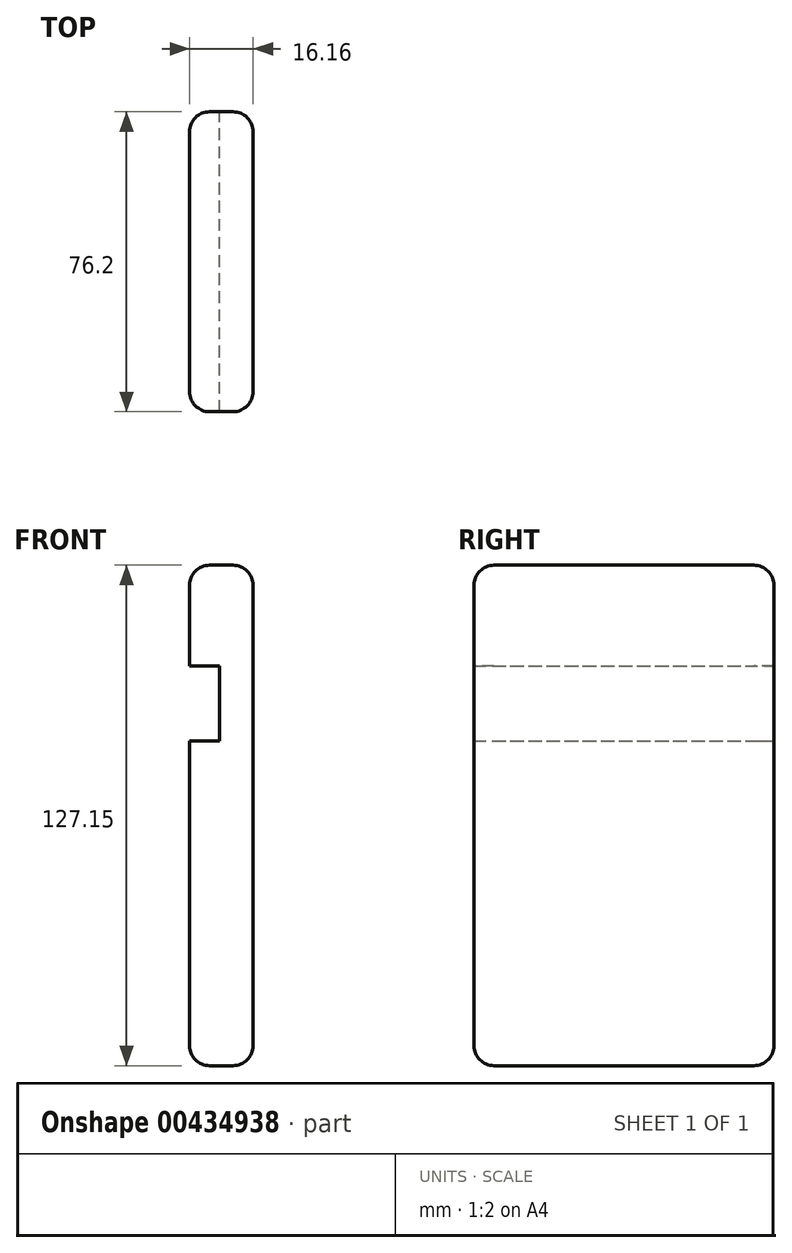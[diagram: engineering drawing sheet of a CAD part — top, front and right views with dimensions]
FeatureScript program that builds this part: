
annotation { "Feature Type Name" : "Feature", "Feature Type Description" : "" }
export const myFeature = defineFeature(function(context is Context, id is Id, definition is map)
    precondition{}
    {
        {
            var Q0;
            Q0=qCreatedBy(makeId("Front.planeOp"),FACE);
            var sketch = newSketch(context, id + "F0", { "sketchPlane" : qUnion([Q0])});
            skLineSegment(sketch, "E0", {"start": v(0, 0) * mm, "end": v(0, 127.15) * mm});
            skLineSegment(sketch, "E1", {"start": v(0, 127.15) * mm, "end": v(-16.16, 127.15) * mm});
            skLineSegment(sketch, "E2", {"start": v(-16.16, 127.15) * mm, "end": v(-16.16, 101.6) * mm});
            skLineSegment(sketch, "E3", {"start": v(-16.16, 101.6) * mm, "end": v(-8.54, 101.6) * mm});
            skLineSegment(sketch, "E4", {"start": v(-8.54, 101.6) * mm, "end": v(-8.54, 82.55) * mm});
            skLineSegment(sketch, "E5", {"start": v(-8.54, 82.55) * mm, "end": v(-16.16, 82.55) * mm});
            skLineSegment(sketch, "E6", {"start": v(-16.16, 82.55) * mm, "end": v(-16.16, 0) * mm});
            skLineSegment(sketch, "E7", {"start": v(-16.16, 0) * mm, "end": v(0, 0) * mm});
            skSolve(sketch);
        }
        {
            var Q0;
            Q0=makeQuery(id+"F0.imprint","IMPRINT",FACE,{"disambiguationData":[TD([[makeQuery(id+"F0.imprint","IMPRINT",EDGE,{"derivedFrom":sQuery(id+"F0.wireOp",EDGE,"E0")}),1.0]])]});
            extrude(context, id + "F1", {"entities" : qUnion([Q0]), "depth" : 76.2 * mm});
        }
        {
            var Q0;
            Q0=makeQuery(id+"F1.opExtrude","CAP_EDGE",EDGE,{"disambiguationData":[OSD([sQuery(id+"F0.wireOp",EDGE,"E1")])],"isStart":false});
            var Q1;
            Q1=makeQuery(id+"F1.opExtrude","SWEPT_FACE",FACE,{"disambiguationData":[OSD([sQuery(id+"F0.wireOp",EDGE,"E0")])]});
            fillet(context, id + "F2", {"entities" : qUnion([Q0, Q1]), "radius" : 5.08 * mm, "tangentPropagation" : true, "allowEdgeOverflow" : false});
        }
        {
            var Q0;
            Q0=makeQuery(id+"F1.opExtrude","CAP_EDGE",EDGE,{"disambiguationData":[OSD([sQuery(id+"F0.wireOp",EDGE,"E6")])],"isStart":false});
            var Q1;
            Q1=makeQuery(id+"F1.opExtrude","CAP_EDGE",EDGE,{"disambiguationData":[OSD([sQuery(id+"F0.wireOp",EDGE,"E6")])],"isStart":true});
            var Q2;
            Q2=makeQuery(id+"F1.opExtrude","SWEPT_EDGE",EDGE,{"disambiguationData":[OSD([sQuery(id+"F0.wireOp",EDGE,"E6"),sQuery(id+"F0.wireOp",EDGE,"E7")])]});
            var Q3;
            Q3=makeQuery(id+"F1.opExtrude","CAP_EDGE",EDGE,{"disambiguationData":[OSD([sQuery(id+"F0.wireOp",EDGE,"E2")])],"isStart":true});
            var Q4;
            Q4=makeQuery(id+"F1.opExtrude","SWEPT_EDGE",EDGE,{"disambiguationData":[OSD([sQuery(id+"F0.wireOp",EDGE,"E1"),sQuery(id+"F0.wireOp",EDGE,"E2")])]});
            fillet(context, id + "F3", {"entities" : qUnion([Q0, Q1, Q2, Q3, Q4]), "radius" : 5.08 * mm, "tangentPropagation" : true, "allowEdgeOverflow" : false});
        }
        {
            var Q0;
            Q0=makeQuery(id+"F1.opExtrude","CAP_EDGE",EDGE,{"disambiguationData":[OSD([sQuery(id+"F0.wireOp",EDGE,"E1")])],"isStart":true});
            var Q1;
            Q1=makeQuery(id+"F1.opExtrude","CAP_EDGE",EDGE,{"disambiguationData":[OSD([sQuery(id+"F0.wireOp",EDGE,"E7")])],"isStart":true});
            var Q2;
            Q2=makeQuery(id+"F1.opExtrude","CAP_EDGE",EDGE,{"disambiguationData":[OSD([sQuery(id+"F0.wireOp",EDGE,"E7")])],"isStart":false});
            fillet(context, id + "F4", {"entities" : qUnion([Q0, Q1, Q2]), "radius" : 5.08 * mm, "tangentPropagation" : true, "allowEdgeOverflow" : false});
        }
    });
